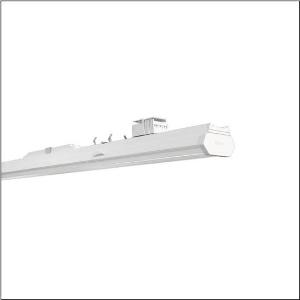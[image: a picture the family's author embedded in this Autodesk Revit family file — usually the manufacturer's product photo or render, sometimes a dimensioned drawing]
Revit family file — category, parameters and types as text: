
# Revit family: licross_r__21_protected_ho_52td12mn4e5m_88f3
name_source: partatom
category: Lighting Fixtures
units: mm (PartAtom-declared; Revit-internal decimal feet)

## family parameters
Cut with Voids When Loaded = No
Host = Face
Light Source = No
Part Type = Normal
Room Calculation Point = No
Round Connector Dimension = Use Diameter
Shared = No

## types (1)
- --- (1 x LED, 14780 lm, 83.2 W, 4000K)
    Apparent Load = 83 VA
    CIE Flux Codes = 70 91 97 98 100
    Color Rendering = 80
    Color Temperature = 4000K
    Default Elevation = 1800 mm
    Description = Licross® 21 Protected HO, luminaire insert, of sheet steel, galvanised, coil coated, white, length: 1.500mm, width: 90mm, height: 101mm, LED rated luminous flux: 14.790lm, light colour: 840, control gear: ON/OFF Multilumen, with plug, 3-pole, with phase selection, mains connection: 220..240V, AC, 50/60Hz, rated input power: 83W, halogen-free wiring, primary light control with lens, of plastic, primary optical cover: cover, of PMMA, light emission: direct distribution, primary light characteristic: symmetric, protection rating (complete): IP54, insulation class (complete): insulation class I (protective earthing), certification: CE, ENEC, VDE, UKCA, protection symbol: D if used in an environment with non-conductive dust loads with corresponding accessories, impact resistance: IK06, permissible ambient temperature for indoor applications: -35..+35°C, corresponds to IFS (International Featured Standards) requirements for safety and quality in the food industry, reducing of maximum allowable ambient temperature of 5°C with ceiling mounting, LABS conformity tested according to VDMA 24364:2018-05, packaging unit: 1 piece
    Height = 92 mm
    Lamp = 1 x LED
    Lamp Light Flux = 14780 lm
    Lamp Power = 83.2 W
    Lamp count = 1
    Length = 1500 mm
    Luminous efficacy = 178 lm/W
    Manufacturer = Siteco
    ModVariant = No
    Model = 52TD12MN4E5M
    Mounting Place = Ceiling
    Mounting Type = Pendant
    Number of Poles = 1
    OnlyDefault = Yes
    Power Factor = 1
    Product Name = Licross® 21 Protected HO
    Product group = luminaire insert
    ProductGroupID = 901
    Protection Class = Protection class I
    Protection Degree = IP 54
    RLX_Detail_Level = 1
    RLX_Emergency_Light_Flux = 0 lm
    RLX_Emergency_Type = 0
    RLX_Emergency_Type_DB = No
    RlxData = <blob elided: 22057 chars, md5=1d5085f6>
    Socket = socket
    Standby Power = 0 W
    System Light Flux = 14780 lm
    System Power = 83 W
    Type Comments = factory setting: luminous flux: 100 % | (A | C | E) | 195 mA
    Type Image = l_1256148.jpg
    URL = http://relux.com
    VarID = @adj_057459
    Voltage = 0 V
    Weight = 0.00 kg
    Width = 88 mm

## geometry (parser evidence)
native form markers: Blend x4, Sweep x9
no freeform markers — native parametric forms only
